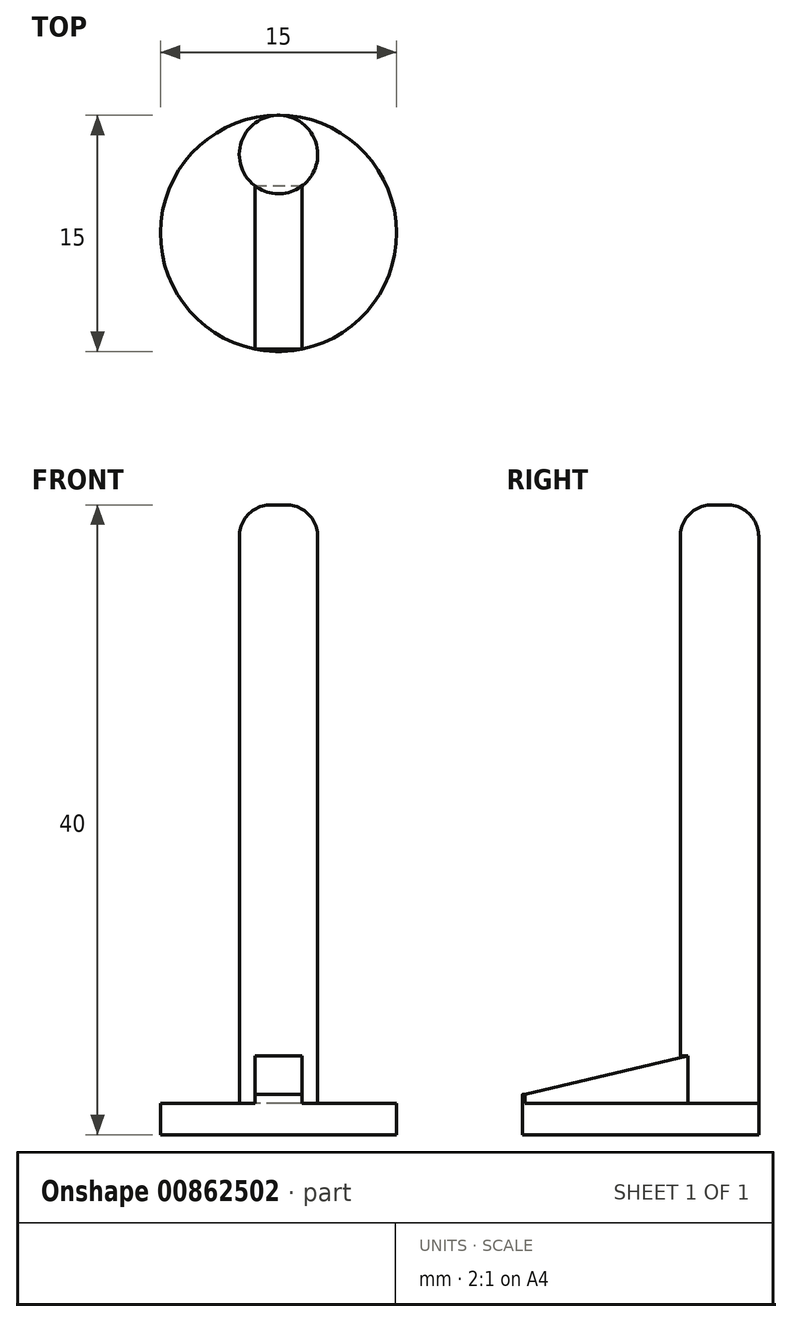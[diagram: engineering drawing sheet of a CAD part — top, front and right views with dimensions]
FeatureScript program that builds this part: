
annotation { "Feature Type Name" : "Feature", "Feature Type Description" : "" }
export const myFeature = defineFeature(function(context is Context, id is Id, definition is map)
    precondition{}
    {
        {
            var Q0;
            Q0=qCreatedBy(makeId("Top.planeOp"),FACE);
            var sketch = newSketch(context, id + "F0", { "sketchPlane" : qUnion([Q0])});
            skCircle(sketch, "E0", {"center": v(0, -7.5) * mm, "radius": 7.5 * mm});
            skLineSegment(sketch, "E1", {"start": v(0, 0) * mm, "end": v(0, -2.5) * mm});
            skSolve(sketch);
        }
        {
            var Q0;
            Q0=makeQuery(id+"F0.imprint","IMPRINT",FACE,{"disambiguationData":[TD([[makeQuery(id+"F0.imprint","IMPRINT",EDGE,{"derivedFrom":sQuery(id+"F0.wireOp",EDGE,"E0")}),1.0]])]});
            var sketch = newSketch(context, id + "F1", { "sketchPlane" : qUnion([Q0])});
            skCircle(sketch, "E2", {"center": v(0, -2.5) * mm, "radius": 2.5 * mm});
            skSolve(sketch);
        }
        {
            var Q0;
            Q0 = qSketchRegion(id + "F1", true);
            extrude(context, id + "F2", {"entities" : qUnion([Q0]), "depth" : 40 * mm, "offsetDistance" : 25 * mm});
        }
        {
            var Q0;
            Q0 = qSketchRegion(id + "F0", true);
            extrude(context, id + "F3", {"entities" : qUnion([Q0]), "operationType" : NewBodyOperationType.ADD, "depth" : 2 * mm, "offsetDistance" : 25 * mm});
        }
        {
            var Q0;
            Q0=makeQuery(id+"F2.opExtrude","CAP_FACE",FACE,{"disambiguationData":[OSD([sQuery(id+"F1.wireOp",EDGE,"E2")])],"isStart":false});
            fillet(context, id + "F4", {"entities" : qUnion([Q0]), "radius" : 2 * mm, "tangentPropagation" : true, "allowEdgeOverflow" : false});
        }
        {
            var Q0;
            Q0=makeQuery(id+"F3.opExtrude","CAP_FACE",FACE,{"disambiguationData":[OSD([sQuery(id+"F0.wireOp",EDGE,"E0")])],"isStart":false});
            var sketch = newSketch(context, id + "F5", { "sketchPlane" : qUnion([Q0])});
            skLineSegment(sketch, "E3.top", {"start": v(-1.5, -4) * mm, "end": v(1.5, -4) * mm});
            skLineSegment(sketch, "E3.left", {"start": v(-1.5, -14.85) * mm, "end": v(-1.5, -4) * mm});
            skLineSegment(sketch, "E3.right", {"start": v(1.5, -14.85) * mm, "end": v(1.5, -4) * mm});
            skCircle(sketch, "E4", {"center": v(0, -7.5) * mm, "radius": 7.5 * mm});
            skPoint(sketch, "E5.orphan", {"position": v(-1.5, -15) * mm});
            skPoint(sketch, "E6.start.orphan", {"position": v(0, -15) * mm});
            skSolve(sketch);
        }
        {
            var Q0;
            {var subQ0=sQuery(id+"F5.wireOp",EDGE,"E4");var subQ1=sQuery(id+"F5.wireOp",EDGE,"E3.left");var subQ2=makeQuery(id+"F5.imprint","INTERSECT",VERTEX,{"derivedFrom":[subQ1,subQ0]});Q0=makeQuery(id+"F5.imprint","IMPRINT",FACE,{"disambiguationData":[TD([[makeQuery(id+"F5.imprint","IMPRINT",EDGE,{"disambiguationData":[TD([[subQ2,-1.0]])],"derivedFrom":subQ0}),1.0]])]});}
            extrude(context, id + "F6", {"entities" : qUnion([Q0]), "operationType" : NewBodyOperationType.ADD, "depth" : 3 * mm, "offsetDistance" : 25 * mm});
        }
        {
            var Q0;
            Q0=makeQuery(id+"F6.opExtrude","SWEPT_FACE",FACE,{"disambiguationData":[OSD([sQuery(id+"F5.wireOp",EDGE,"E3.right")])]});
            var sketch = newSketch(context, id + "F7", { "sketchPlane" : qUnion([Q0])});
            skLineSegment(sketch, "E7", {"start": v(-4.48, 5) * mm, "end": v(-14.85, 2.57) * mm});
            skLineSegment(sketch, "E8", {"start": v(-14.85, 2.57) * mm, "end": v(-17.07, 2.57) * mm});
            skLineSegment(sketch, "E9", {"start": v(-17.07, 2.57) * mm, "end": v(-17.07, 6.12) * mm});
            skLineSegment(sketch, "E10", {"start": v(-17.07, 6.12) * mm, "end": v(-14.85, 5) * mm});
            skLineSegment(sketch, "E11", {"start": v(-14.85, 5) * mm, "end": v(-4.48, 5) * mm});
            skSolve(sketch);
        }
        {
            var Q0;
            {var subQ0=sQuery(id+"F7.wireOp",EDGE,"E8");Q0=makeQuery(id+"F7.imprint","IMPRINT",FACE,{"disambiguationData":[TD([[makeQuery(id+"F7.imprint","IMPRINT",EDGE,{"derivedFrom":subQ0}),-1.0]])]});}
            var Q1;
            {var subQ0=sQuery(id+"F7.wireOp",EDGE,"E7");Q1=makeQuery(id+"F7.imprint","IMPRINT",FACE,{"disambiguationData":[TD([[makeQuery(id+"F7.imprint","IMPRINT",EDGE,{"derivedFrom":subQ0}),-1.0]])]});}
            extrude(context, id + "F8", {"entities" : qUnion([Q0, Q1]), "operationType" : NewBodyOperationType.REMOVE, "endBound" : BoundingType.THROUGH_ALL, "oppositeDirection" : true, "depth" : 25 * mm, "offsetDistance" : 25 * mm});
        }
    });
